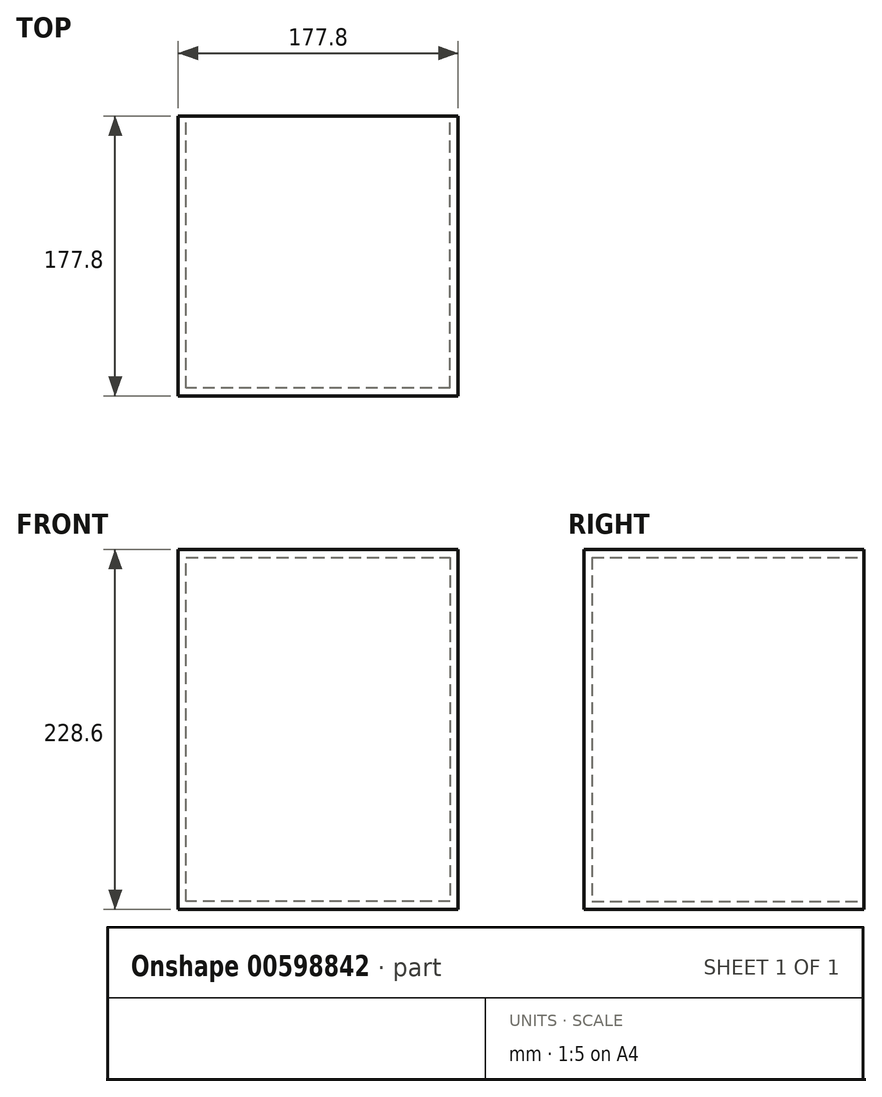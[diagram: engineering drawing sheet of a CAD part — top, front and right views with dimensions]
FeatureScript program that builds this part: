
annotation { "Feature Type Name" : "Feature", "Feature Type Description" : "" }
export const myFeature = defineFeature(function(context is Context, id is Id, definition is map)
    precondition{}
    {
        {
            var Q0;
            Q0=qCreatedBy(makeId("Front.planeOp"),FACE);
            var sketch = newSketch(context, id + "F0", { "sketchPlane" : qUnion([Q0])});
            skLineSegment(sketch, "E0.bottom", {"start": v(88.9, 114.3) * mm, "end": v(-88.9, 114.3) * mm});
            skLineSegment(sketch, "E0.top", {"start": v(88.9, -114.3) * mm, "end": v(-88.9, -114.3) * mm});
            skLineSegment(sketch, "E0.left", {"start": v(88.9, 114.3) * mm, "end": v(88.9, -114.3) * mm});
            skLineSegment(sketch, "E0.right", {"start": v(-88.9, 114.3) * mm, "end": v(-88.9, -114.3) * mm});
            skPoint(sketch, "E0.middle", {"position": v(0, 0) * mm});
            skSolve(sketch);
        }
        {
            var Q0;
            Q0=makeQuery(id+"F0.imprint","IMPRINT",FACE,{"disambiguationData":[TD([[makeQuery(id+"F0.imprint","IMPRINT",EDGE,{"derivedFrom":sQuery(id+"F0.wireOp",EDGE,"E0.bottom")}),1.0]])]});
            extrude(context, id + "F1", {"entities" : qUnion([Q0]), "depth" : 177.8 * mm, "offsetDistance" : 25.4 * mm});
        }
        {
            var Q0;
            Q0=makeQuery(id+"F1.opExtrude","CAP_FACE",FACE,{"disambiguationData":[OSD([sQuery(id+"F0.wireOp",EDGE,"E0.bottom"),sQuery(id+"F0.wireOp",EDGE,"E0.top"),sQuery(id+"F0.wireOp",EDGE,"E0.left"),sQuery(id+"F0.wireOp",EDGE,"E0.right")])],"isStart":true});
            var sketch = newSketch(context, id + "F2", { "sketchPlane" : qUnion([Q0])});
            skLineSegment(sketch, "E1.0", {"start": v(-83.82, -109.22) * mm, "end": v(83.82, -109.22) * mm});
            skLineSegment(sketch, "E1.1", {"start": v(-83.82, 109.22) * mm, "end": v(-83.82, -109.22) * mm});
            skLineSegment(sketch, "E1.2", {"start": v(83.82, 109.22) * mm, "end": v(-83.82, 109.22) * mm});
            skLineSegment(sketch, "E1.3", {"start": v(83.82, -109.22) * mm, "end": v(83.82, 109.22) * mm});
            skSolve(sketch);
        }
        {
            var Q0;
            Q0=makeQuery(id+"F2.imprint","IMPRINT",FACE,{"disambiguationData":[TD([[makeQuery(id+"F2.imprint","IMPRINT",EDGE,{"derivedFrom":sQuery(id+"F2.wireOp",EDGE,"E1.0")}),1.0]])]});
            extrude(context, id + "F3", {"entities" : qUnion([Q0]), "operationType" : NewBodyOperationType.REMOVE, "oppositeDirection" : true, "depth" : 172.72 * mm, "offsetDistance" : 25.4 * mm});
        }
    });
